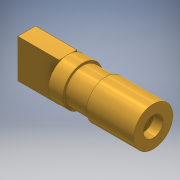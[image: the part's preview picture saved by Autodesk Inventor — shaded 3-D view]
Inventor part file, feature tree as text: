
AUTODESK INVENTOR PART (.ipt)
format: ipt  version: 2016 (Build 200138000, 138)  size: 131,584 bytes
history: native  units: mm
features: sketch x2, revolve x1, extrude x1
ambient origin geometry x8: Origin, YZ Plane, XZ Plane, XY Plane, X Axis, Y Axis, Z Axis, Center Point
bodies: Solid1 (feature_tree)
feature tree (4):
  revolve  "Revolution1"  [1 undecoded]
  extrude  "Extrusion1"  Depth=6.3mm
  sketch  "Sketch1"  dims[d0=7.2mm d1=5.98mm]
  sketch  "Sketch2"  dims[d2=2.26mm d3=6.05mm d4=3.0mm d5=1.5mm d6=13.0mm d7=5.4mm d8=90.0deg d9=5.9mm d10=2.7mm d11=6.3mm d12=0.0mm]
note: 1 required parameter value undecoded (feature->parameter linkage not recoverable at this tier; creation-order binding heuristic only, values carry confidence <= 0.55)
